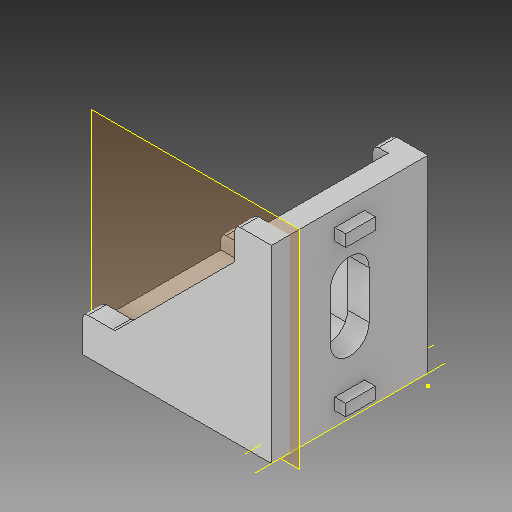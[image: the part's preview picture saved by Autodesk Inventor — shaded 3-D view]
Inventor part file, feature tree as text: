
AUTODESK INVENTOR PART (.ipt)
format: ipt  version: 2017 (Build 210142000, 142)  size: 179,712 bytes
history: native  units: mm
features: sketch x8, other x5, plane x1
ambient origin geometry x8: Origin, YZ Plane, XZ Plane, XY Plane, X Axis, Y Axis, Z Axis, Center Point
bodies: Solid1 (feature_tree)
feature tree (14):
  other  "30mm Bracket_CPY_MIR2.ipt"
  other  "Solid1::30mm Bracket_CPY_MIR2.ipt"
  other  "TaggingFeature1"
  sketch  "Sketch1"  dims[d0=10.0mm]
  sketch  "Sketch2"
  sketch  "Sketch3"
  sketch  "Sketch4"
  sketch  "Sketch5"
  sketch  "Sketch7"
  sketch  "Sketch9"
  sketch  "Sketch10"
  plane  "Work Plane1"
  other  "Work Axis1"
  other  "Work Axis2"
